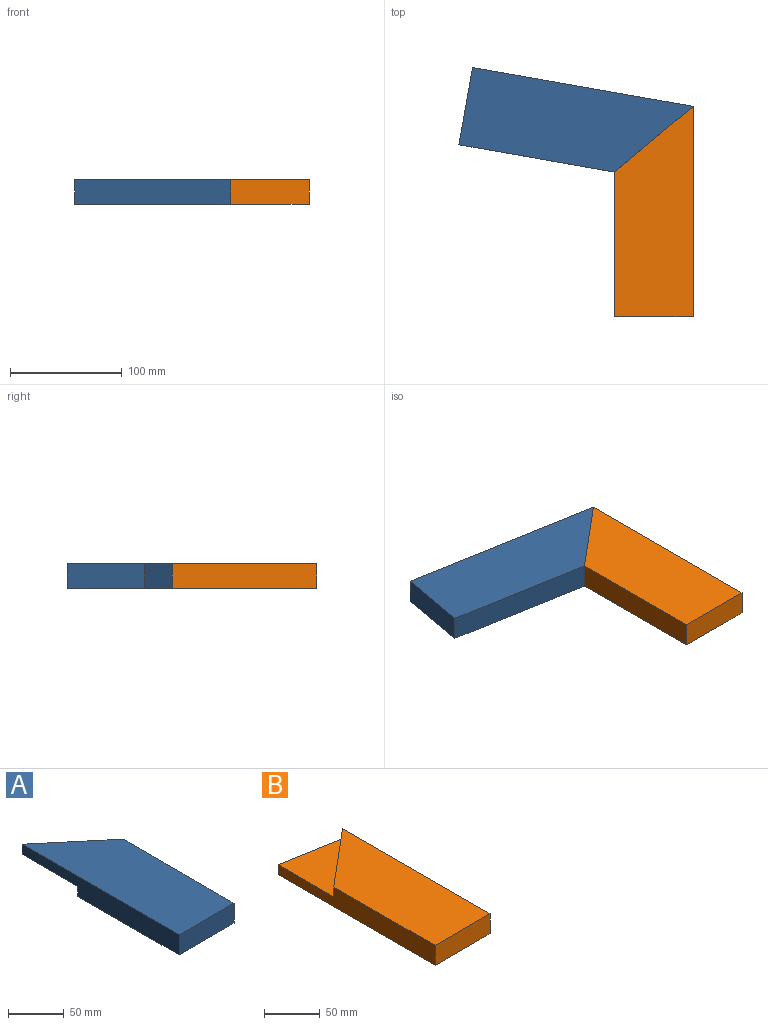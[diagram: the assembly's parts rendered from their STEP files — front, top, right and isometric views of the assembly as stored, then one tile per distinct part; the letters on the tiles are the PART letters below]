
ASSEMBLY  parts=2 mates=1
PART A: 8 faces, bbox 70x200x22 mm
  f0: plane 141.26x70mm, normal (0,0,-1), area 9456.4mm2, adj f1,f2,f3,f6
  f1: plane 200x22mm, normal (-1,0,0), area 3618.1mm2, adj f0,f2,f4,f5,f6,f7
  f2: plane 70x22mm, normal (0,-1,0), area 1540mm2, adj f0,f1,f3,f4
  f3: plane 141.26x22mm, normal (1,0,0), area 3107.8mm2, adj f0,f2,f4,f5,f6
  f4: plane 200x70mm, normal (0,0,1), area 11944.2mm2, adj f1,f2,f3,f5
  f5: plane 70x58.74mm, normal (0.64,0.77,0), area 1005.2mm2, adj f1,f3,f4,f7
  f6: plane 70x12.34mm, normal (-0.17,0.98,0), area 781.9mm2, adj f0,f1,f3,f7
  f7: plane 71.08x70mm, normal (0,0,-1), area 2487.8mm2, adj f1,f5,f6
PART B: 8 faces, bbox 69.9x200x22 mm
  f0: plane 69.92x12.33mm, normal (0.17,0.98,0), area 781mm2, adj f1,f4,f5,f7
  f1: plane 200x22mm, normal (-1,0,0), area 3619mm2, adj f0,f2,f3,f5,f6,f7
  f2: plane 187.67x69.92mm, normal (0,0,1), area 11071mm2, adj f1,f3,f4,f6
  f3: plane 69.92x22mm, normal (0,-1,0), area 1538.3mm2, adj f1,f2,f4,f5
  f4: plane 187.67x22mm, normal (1,0,0), area 4128.8mm2, adj f0,f2,f3,f5,f6
  f5: plane 200x69.92mm, normal (0,0,-1), area 13553.2mm2, adj f0,f1,f3,f4
  f6: plane 69.92x58.67mm, normal (-0.64,0.77,0), area 1004mm2, adj f1,f2,f4,f7
  f7: plane 71x69.92mm, normal (0,0,1), area 2482.2mm2, adj f0,f1,f6
PLACE A rot(axis=(0,0,-1),100deg) t=(-175.83,120.16,0.72)mm
PLACE B t=(-30.35,11.71,0.72)mm
MATE fastened B.f6 <-> A.f5  axis (-0.64,0.77,0) through (-116.63,68.68,22.72)mm
